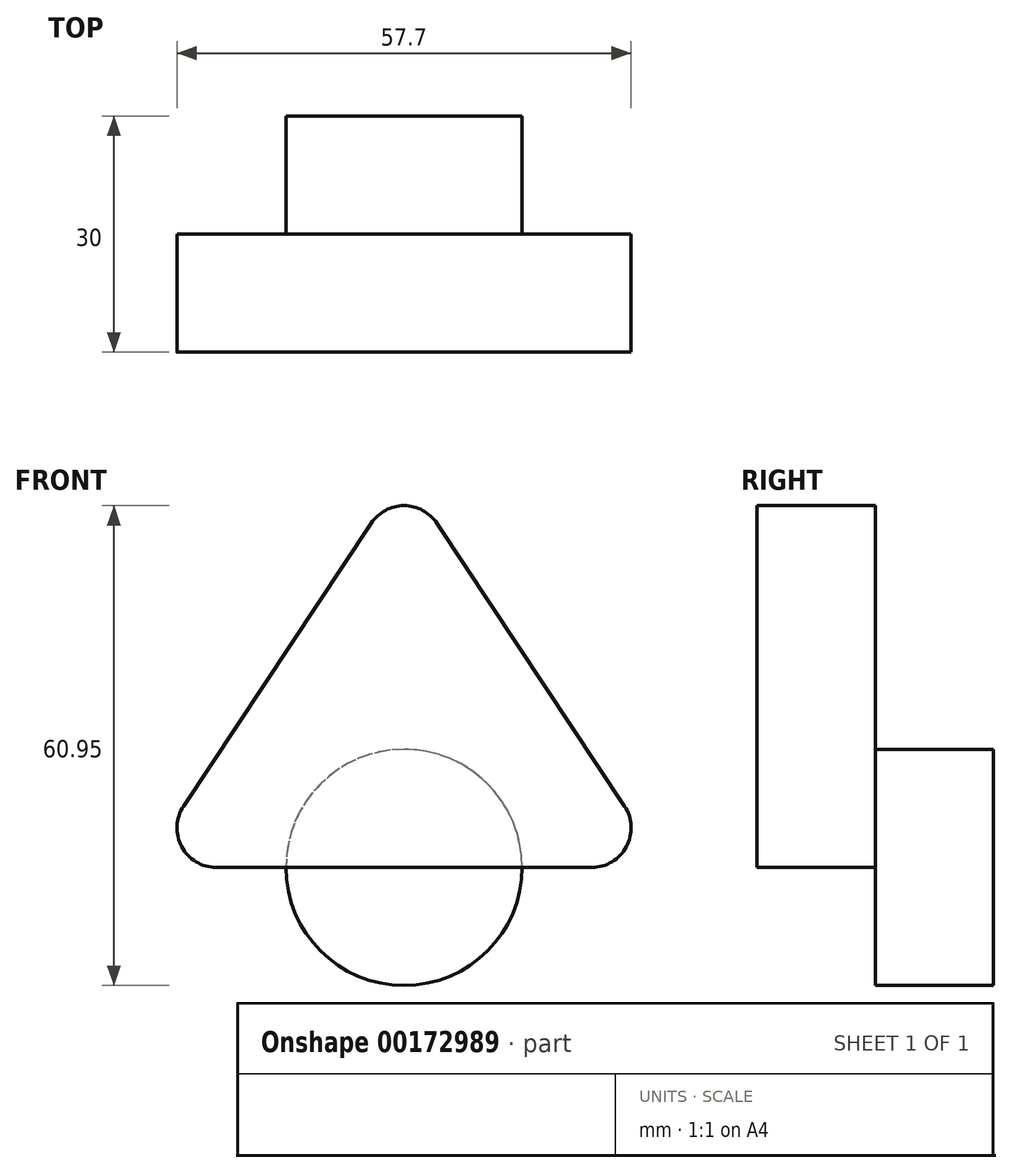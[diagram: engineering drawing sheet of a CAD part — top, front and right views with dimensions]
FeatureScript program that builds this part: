
annotation { "Feature Type Name" : "Feature", "Feature Type Description" : "" }
export const myFeature = defineFeature(function(context is Context, id is Id, definition is map)
    precondition{}
    {
        {
            var Q0;
            Q0=qCreatedBy(makeId("Front.planeOp"),FACE);
            var sketch = newSketch(context, id + "F0", { "sketchPlane" : qUnion([Q0])});
            skLineSegment(sketch, "E0", {"start": v(-33.17, 0) * mm, "end": v(33.17, 0) * mm});
            skLineSegment(sketch, "E1", {"start": v(33.17, 0) * mm, "end": v(0, 50) * mm});
            skLineSegment(sketch, "E2", {"start": v(0, 50) * mm, "end": v(-33.17, 0) * mm});
            skLineSegment(sketch, "E3", {"start": v(-33.17, 0) * mm, "end": v(33.17, 0) * mm, "construction": true});
            skSolve(sketch);
        }
        {
            var Q0;
            Q0 = qSketchRegion(id + "F0", true);
            extrude(context, id + "F1", {"entities" : qUnion([Q0]), "depth" : 15 * mm});
        }
        {
            var Q0;
            Q0=makeQuery(id+"F1.opExtrude","CAP_FACE",FACE,{"disambiguationData":[OSD([sQuery(id+"F0.wireOp",EDGE,"E1"),sQuery(id+"F0.wireOp",EDGE,"E2"),sQuery(id+"F0.wireOp",EDGE,"23cc51e6-d652-4618-8b75-c2b7b54aa3980.MirrorCS"),sQuery(id+"F0.wireOp",EDGE,"de5c65d5-f411-4725-88b2-4a877b177b780.MirrorCS")])],"isStart":true});
            var sketch = newSketch(context, id + "F2", { "sketchPlane" : qUnion([Q0])});
            skCircle(sketch, "E4", {"center": v(0, 0) * mm, "radius": 15 * mm});
            skSolve(sketch);
        }
        {
            var Q0;
            Q0 = qSketchRegion(id + "F2", true);
            extrude(context, id + "F3", {"entities" : qUnion([Q0]), "operationType" : NewBodyOperationType.ADD, "depth" : 15 * mm});
        }
        {
            var Q0;
            Q0=makeQuery(id+"F1.opExtrude","SWEPT_EDGE",EDGE,{"disambiguationData":[OSD([sQuery(id+"F0.wireOp",EDGE,"E1"),sQuery(id+"F0.wireOp",EDGE,"E2")])]});
            fillet(context, id + "F4", {"entities" : qUnion([Q0]), "radius" : 5 * mm, "tangentPropagation" : true, "allowEdgeOverflow" : false});
        }
        {
            var Q0;
            Q0=makeQuery(id+"F1.opExtrude","SWEPT_EDGE",EDGE,{"disambiguationData":[OSD([sQuery(id+"F0.wireOp",EDGE,"E0"),sQuery(id+"F0.wireOp",EDGE,"E1")])]});
            var Q1;
            Q1=makeQuery(id+"F1.opExtrude","SWEPT_EDGE",EDGE,{"disambiguationData":[OSD([sQuery(id+"F0.wireOp",EDGE,"E0"),sQuery(id+"F0.wireOp",EDGE,"E2")])]});
            fillet(context, id + "F5", {"entities" : qUnion([Q0, Q1]), "radius" : 5 * mm, "tangentPropagation" : true, "allowEdgeOverflow" : false});
        }
    });
